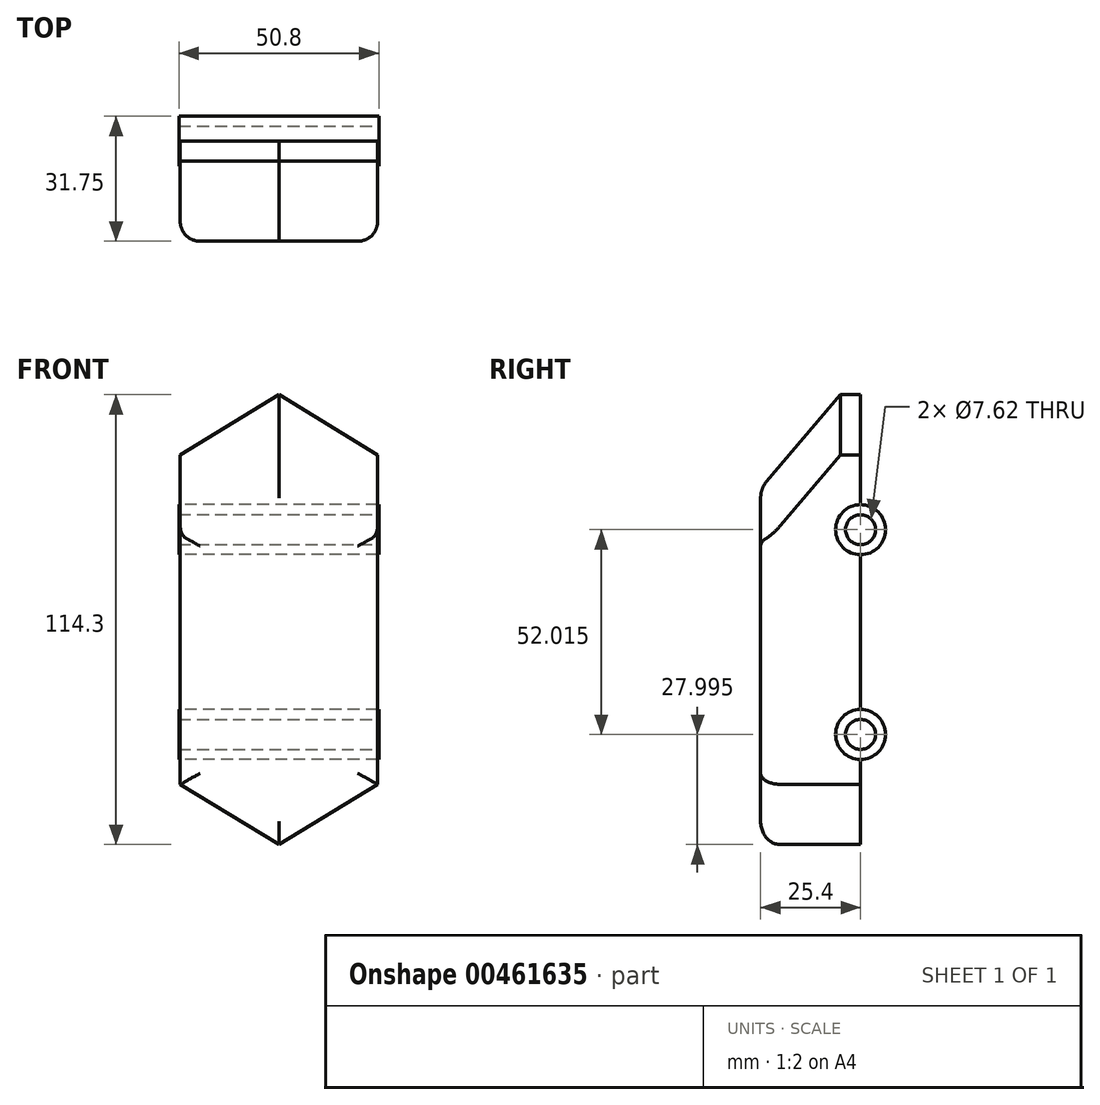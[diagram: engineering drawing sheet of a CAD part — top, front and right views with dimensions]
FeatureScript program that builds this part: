
annotation { "Feature Type Name" : "Feature", "Feature Type Description" : "" }
export const myFeature = defineFeature(function(context is Context, id is Id, definition is map)
    precondition{}
    {
        {
            var Q0;
            Q0=qCreatedBy(makeId("Front.planeOp"),FACE);
            var sketch = newSketch(context, id + "F0", { "sketchPlane" : qUnion([Q0])});
            skLineSegment(sketch, "E0", {"start": v(-25.08, 41.85) * mm, "end": v(0, 57.15) * mm});
            skLineSegment(sketch, "E1.MirrorCS", {"start": v(-25.08, -41.85) * mm, "end": v(0, -57.15) * mm});
            skLineSegment(sketch, "E2", {"start": v(-25.08, 41.85) * mm, "end": v(-25.08, -41.85) * mm});
            skLineSegment(sketch, "E3.MirrorCS", {"start": v(25.08, -41.85) * mm, "end": v(0, -57.15) * mm});
            skLineSegment(sketch, "E4.MirrorCS", {"start": v(25.08, 41.85) * mm, "end": v(25.08, -41.85) * mm});
            skLineSegment(sketch, "E5.MirrorCS", {"start": v(25.08, 41.85) * mm, "end": v(0, 57.15) * mm});
            skSolve(sketch);
        }
        {
            var Q0;
            Q0 = qSketchRegion(id + "F0", true);
            extrude(context, id + "F1", {"entities" : qUnion([Q0]), "depth" : 25.4 * mm});
        }
        {
            var Q0;
            Q0=makeQuery(id+"F1.opExtrude","CAP_EDGE",EDGE,{"disambiguationData":[OSD([sQuery(id+"F0.wireOp",EDGE,"E0")])],"isStart":false});
            var Q1;
            Q1=makeQuery(id+"F1.opExtrude","CAP_EDGE",EDGE,{"disambiguationData":[OSD([sQuery(id+"F0.wireOp",EDGE,"E5.MirrorCS")])],"isStart":false});
            chamfer(context, id + "F2", {"entities" : qUnion([Q0, Q1]), "width" : 20.32 * mm, "tangentPropagation" : true});
        }
        {
            var Q0;
            Q0=qCreatedBy(makeId("Right.planeOp"),FACE);
            var sketch = newSketch(context, id + "F3", { "sketchPlane" : qUnion([Q0])});
            skCircle(sketch, "E6", {"center": v(0, -29.15) * mm, "radius": 6.35 * mm});
            skCircle(sketch, "E7", {"center": v(0, 22.86) * mm, "radius": 6.35 * mm});
            skSolve(sketch);
        }
        {
            var Q0;
            Q0 = qSketchRegion(id + "F3", true);
            extrude(context, id + "F4", {"entities" : qUnion([Q0]), "operationType" : NewBodyOperationType.REMOVE, "depth" : 46.23 * mm, "hasSecondDirection" : true, "secondDirectionOppositeDirection" : true, "secondDirectionDepth" : 59.18 * mm});
        }
        {
            var Q0;
            Q0=qCreatedBy(makeId("Right.planeOp"),FACE);
            var sketch = newSketch(context, id + "F5", { "sketchPlane" : qUnion([Q0])});
            skCircle(sketch, "E8", {"center": v(0, -29.15) * mm, "radius": 6.35 * mm});
            skSolve(sketch);
        }
        {
            var Q0;
            Q0 = qSketchRegion(id + "F5", true);
            extrude(context, id + "F6", {"entities" : qUnion([Q0]), "operationType" : NewBodyOperationType.ADD, "oppositeDirection" : true, "depth" : 25.4 * mm, "hasSecondDirection" : true, "secondDirectionOppositeDirection" : false, "secondDirectionDepth" : 25.4 * mm});
        }
        {
            var Q0;
            Q0=qCreatedBy(makeId("Right.planeOp"),FACE);
            var sketch = newSketch(context, id + "F7", { "sketchPlane" : qUnion([Q0])});
            skCircle(sketch, "E9", {"center": v(0, -29.15) * mm, "radius": 3.81 * mm});
            skSolve(sketch);
        }
        {
            var Q0;
            Q0 = qSketchRegion(id + "F7", true);
            extrude(context, id + "F8", {"entities" : qUnion([Q0]), "operationType" : NewBodyOperationType.REMOVE, "oppositeDirection" : true, "depth" : 46.23 * mm, "hasSecondDirection" : true, "secondDirectionOppositeDirection" : false, "secondDirectionDepth" : 55.88 * mm});
        }
        {
            var Q0;
            Q0=qCreatedBy(makeId("Right.planeOp"),FACE);
            var sketch = newSketch(context, id + "F9", { "sketchPlane" : qUnion([Q0])});
            skCircle(sketch, "E10", {"center": v(0, 22.86) * mm, "radius": 6.35 * mm});
            skSolve(sketch);
        }
        {
            var Q0;
            Q0=makeQuery(id+"F9.imprint","IMPRINT",FACE,{"disambiguationData":[TD([[makeQuery(id+"F9.imprint","IMPRINT",EDGE,{"derivedFrom":sQuery(id+"F9.wireOp",EDGE,"E10")}),1.0]])]});
            extrude(context, id + "F10", {"entities" : qUnion([Q0]), "operationType" : NewBodyOperationType.ADD, "depth" : 25.4 * mm, "hasSecondDirection" : true, "secondDirectionOppositeDirection" : true, "secondDirectionDepth" : 25.4 * mm});
        }
        {
            var Q0;
            Q0=qCreatedBy(makeId("Right.planeOp"),FACE);
            var sketch = newSketch(context, id + "F11", { "sketchPlane" : qUnion([Q0])});
            skCircle(sketch, "E11", {"center": v(0, 22.86) * mm, "radius": 3.81 * mm});
            skSolve(sketch);
        }
        {
            var Q0;
            Q0 = qSketchRegion(id + "F11", true);
            extrude(context, id + "F12", {"entities" : qUnion([Q0]), "operationType" : NewBodyOperationType.REMOVE, "oppositeDirection" : true, "depth" : 41.4 * mm, "hasSecondDirection" : true, "secondDirectionOppositeDirection" : false, "secondDirectionDepth" : 45.2 * mm});
        }
        {
            var Q0;
            Q0=makeQuery(id+"F1.opExtrude","CAP_FACE",FACE,{"disambiguationData":[OSD([sQuery(id+"F0.wireOp",EDGE,"E0"),sQuery(id+"F0.wireOp",EDGE,"E1.MirrorCS"),sQuery(id+"F0.wireOp",EDGE,"E2"),sQuery(id+"F0.wireOp",EDGE,"E3.MirrorCS"),sQuery(id+"F0.wireOp",EDGE,"E4.MirrorCS"),sQuery(id+"F0.wireOp",EDGE,"E5.MirrorCS")])],"isStart":false});
            fillet(context, id + "F13", {"entities" : qUnion([Q0]), "radius" : 5.08 * mm, "tangentPropagation" : true, "allowEdgeOverflow" : false});
        }
    });
